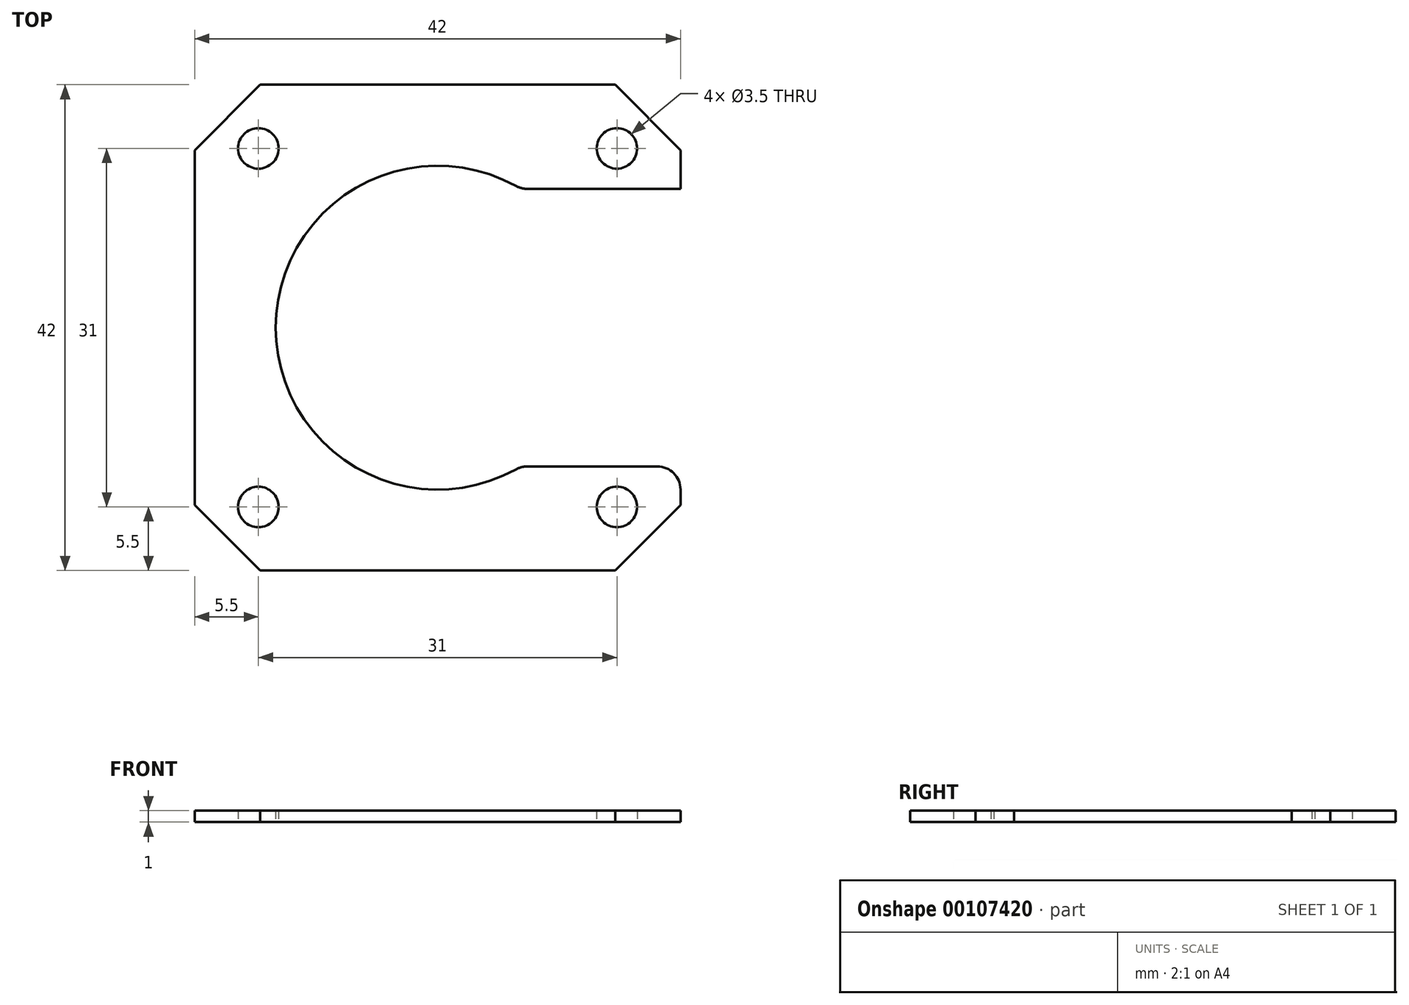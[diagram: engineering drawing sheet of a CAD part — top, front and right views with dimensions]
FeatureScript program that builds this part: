
annotation { "Feature Type Name" : "Feature", "Feature Type Description" : "" }
export const myFeature = defineFeature(function(context is Context, id is Id, definition is map)
    precondition{}
    {
        {
            var Q0;
            Q0=qCreatedBy(makeId("Top.planeOp"),FACE);
            var sketch = newSketch(context, id + "F0", { "sketchPlane" : qUnion([Q0])});
            skCircle(sketch, "E0", {"center": v(0, 0) * mm, "radius": 14 * mm});
            skLineSegment(sketch, "E1.bottom", {"start": v(-15.34, 21) * mm, "end": v(15.34, 21) * mm});
            skLineSegment(sketch, "E1.top", {"start": v(-15.34, -21) * mm, "end": v(15.34, -21) * mm});
            skLineSegment(sketch, "E1.left", {"start": v(-21, 15.34) * mm, "end": v(-21, -15.34) * mm});
            skLineSegment(sketch, "E1.right", {"start": v(21, 15.34) * mm, "end": v(21, -15.34) * mm});
            skLineSegment(sketch, "E2", {"start": v(-21, 15.34) * mm, "end": v(-15.34, 21) * mm});
            skLineSegment(sketch, "E3", {"start": v(15.34, 21) * mm, "end": v(21, 15.34) * mm});
            skLineSegment(sketch, "E4", {"start": v(21, -15.34) * mm, "end": v(15.34, -21) * mm});
            skLineSegment(sketch, "E5", {"start": v(-15.34, -21) * mm, "end": v(-21, -15.34) * mm});
            skLineSegment(sketch, "E6", {"start": v(-18.17, 18.17) * mm, "end": v(18.17, -18.17) * mm, "construction": true});
            skLineSegment(sketch, "E7", {"start": v(-18.17, -18.17) * mm, "end": v(18.17, 18.17) * mm, "construction": true});
            skCircle(sketch, "E8", {"center": v(-15.5, 15.5) * mm, "radius": 1.75 * mm});
            skCircle(sketch, "E9", {"center": v(15.5, 15.5) * mm, "radius": 1.75 * mm});
            skCircle(sketch, "E10", {"center": v(15.5, -15.5) * mm, "radius": 1.75 * mm});
            skCircle(sketch, "E11", {"center": v(-15.5, -15.5) * mm, "radius": 1.75 * mm});
            skLineSegment(sketch, "E12", {"start": v(-15.5, 15.5) * mm, "end": v(-15.5, -15.5) * mm, "construction": true});
            skLineSegment(sketch, "E13", {"start": v(15.5, -15.5) * mm, "end": v(15.5, 15.5) * mm, "construction": true});
            skLineSegment(sketch, "E14", {"start": v(-15.5, 15.5) * mm, "end": v(15.5, 15.5) * mm, "construction": true});
            skLineSegment(sketch, "E15", {"start": v(-15.5, -15.5) * mm, "end": v(15.5, -15.5) * mm, "construction": true});
            skSolve(sketch);
        }
        {
            var Q0;
            Q0 = qSketchRegion(id + "F0", true);
            extrude(context, id + "F1", {"entities" : qUnion([Q0]), "depth" : 1 * mm});
        }
        {
            var Q0;
            Q0=makeQuery(id+"F1.opExtrude","CAP_FACE",FACE,{"disambiguationData":[OSD([sQuery(id+"F0.wireOp",EDGE,"E0"),sQuery(id+"F0.wireOp",EDGE,"E1.bottom"),sQuery(id+"F0.wireOp",EDGE,"E1.top"),sQuery(id+"F0.wireOp",EDGE,"E1.left"),sQuery(id+"F0.wireOp",EDGE,"E1.right"),sQuery(id+"F0.wireOp",EDGE,"E2"),sQuery(id+"F0.wireOp",EDGE,"E3"),sQuery(id+"F0.wireOp",EDGE,"E4"),sQuery(id+"F0.wireOp",EDGE,"E5"),sQuery(id+"F0.wireOp",EDGE,"E8"),sQuery(id+"F0.wireOp",EDGE,"E9"),sQuery(id+"F0.wireOp",EDGE,"E10"),sQuery(id+"F0.wireOp",EDGE,"E11")])],"isStart":false});
            var sketch = newSketch(context, id + "F2", { "sketchPlane" : qUnion([Q0])});
            skLineSegment(sketch, "E16.bottom", {"start": v(21, 12) * mm, "end": v(0, 12) * mm});
            skLineSegment(sketch, "E16.top", {"start": v(21, -12) * mm, "end": v(0, -12) * mm});
            skLineSegment(sketch, "E16.left", {"start": v(21, 12) * mm, "end": v(21, -12) * mm});
            skLineSegment(sketch, "E16.right", {"start": v(0, 12) * mm, "end": v(0, -12) * mm});
            skSolve(sketch);
        }
        {
            var Q0;
            Q0 = qSketchRegion(id + "F2", true);
            extrude(context, id + "F3", {"entities" : qUnion([Q0]), "operationType" : NewBodyOperationType.REMOVE, "endBound" : BoundingType.THROUGH_ALL, "oppositeDirection" : true, "depth" : 25 * mm});
        }
        {
            var Q0;
            Q0=makeQuery(id+"F3.boolean.opBoolean","INTERSECT",EDGE,{"derivedFrom":[makeQuery(id+"F1.opExtrude","SWEPT_FACE",FACE,{"disambiguationData":[OSD([sQuery(id+"F0.wireOp",EDGE,"E0")])]}),makeQuery(id+"F3.opExtrude","SWEPT_FACE",FACE,{"disambiguationData":[OSD([sQuery(id+"F2.wireOp",EDGE,"E16.bottom")])]})]});
            var Q1;
            Q1=makeQuery(id+"F3.boolean.opBoolean","COPY",EDGE,{"derivedFrom":makeQuery(id+"F3.opExtrude","SWEPT_EDGE",EDGE,{"disambiguationData":[OSD([sQuery(id+"F0.wireOp",EDGE,"E1.right"),sQuery(id+"F2.wireOp",EDGE,"E16.bottom"),sQuery(id+"F2.wireOp",EDGE,"E16.left")])]})});
            var Q2;
            Q2=makeQuery(id+"F3.boolean.opBoolean","COPY",EDGE,{"derivedFrom":makeQuery(id+"F3.opExtrude","SWEPT_EDGE",EDGE,{"disambiguationData":[OSD([sQuery(id+"F0.wireOp",EDGE,"E1.right"),sQuery(id+"F2.wireOp",EDGE,"E16.top"),sQuery(id+"F2.wireOp",EDGE,"E16.left")])]})});
            var Q3;
            Q3=makeQuery(id+"F3.boolean.opBoolean","INTERSECT",EDGE,{"derivedFrom":[makeQuery(id+"F1.opExtrude","SWEPT_FACE",FACE,{"disambiguationData":[OSD([sQuery(id+"F0.wireOp",EDGE,"E0")])]}),makeQuery(id+"F3.opExtrude","SWEPT_FACE",FACE,{"disambiguationData":[OSD([sQuery(id+"F2.wireOp",EDGE,"E16.top")])]})]});
            fillet(context, id + "F4", {"entities" : qUnion([Q0, Q1, Q2, Q3]), "radius" : 2 * mm, "tangentPropagation" : true, "allowEdgeOverflow" : false});
        }
    });
